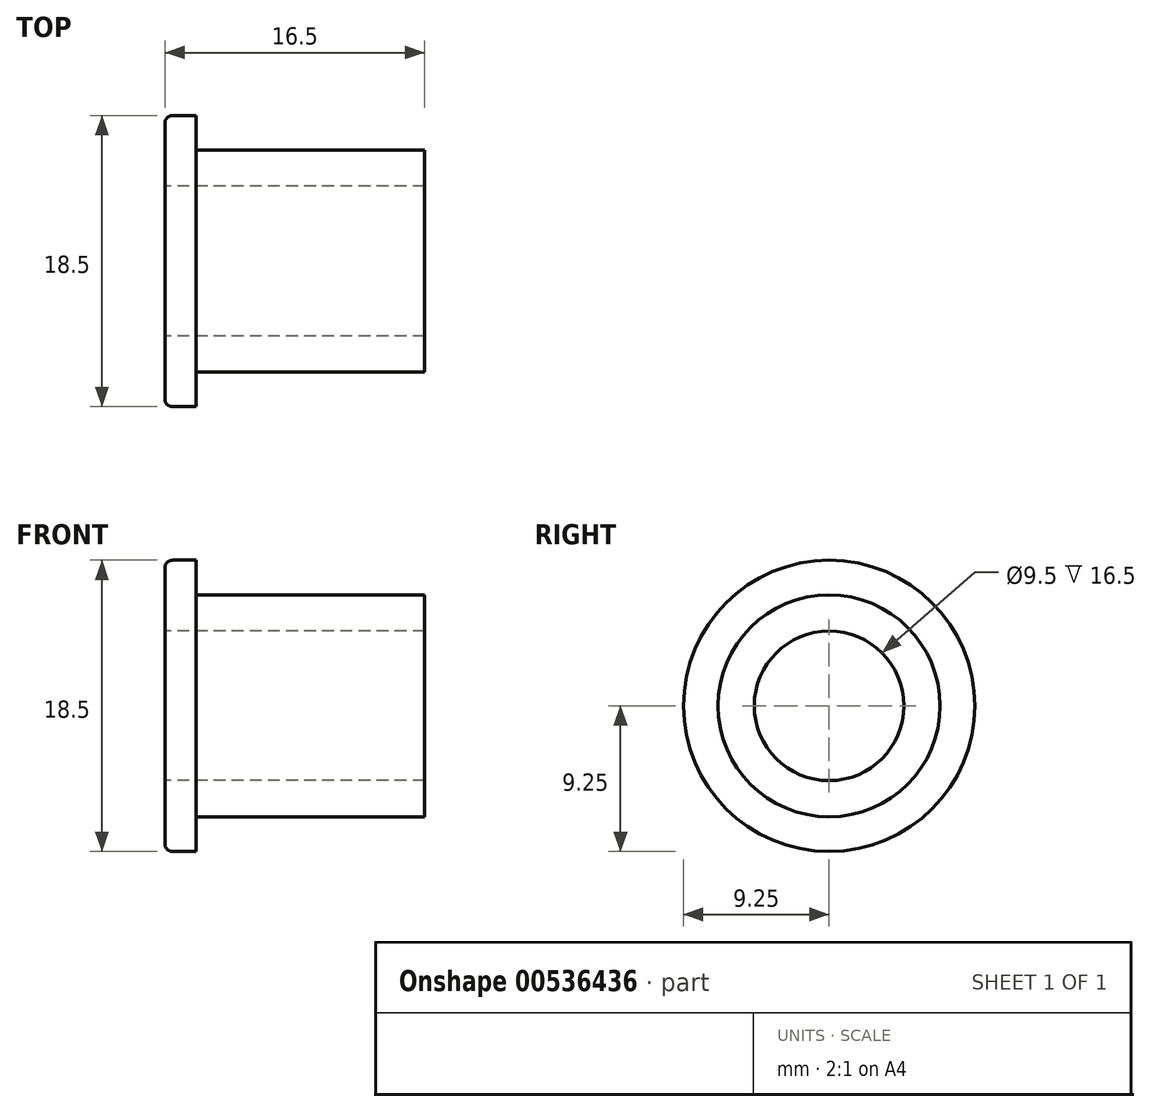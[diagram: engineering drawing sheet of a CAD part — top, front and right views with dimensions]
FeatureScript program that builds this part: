
annotation { "Feature Type Name" : "Feature", "Feature Type Description" : "" }
export const myFeature = defineFeature(function(context is Context, id is Id, definition is map)
    precondition{}
    {
        {
            var Q0;
            Q0=qCreatedBy(makeId("Front.planeOp"),FACE);
            var sketch = newSketch(context, id + "F0", { "sketchPlane" : qUnion([Q0])});
            skLineSegment(sketch, "E0", {"start": v(0, 4.75) * mm, "end": v(0, 9.25) * mm});
            skLineSegment(sketch, "E1", {"start": v(0, 9.25) * mm, "end": v(2, 9.25) * mm});
            skLineSegment(sketch, "E2", {"start": v(2, 9.25) * mm, "end": v(2, 7.05) * mm});
            skLineSegment(sketch, "E3", {"start": v(2, 7.05) * mm, "end": v(16.5, 7.05) * mm});
            skLineSegment(sketch, "E4", {"start": v(16.5, 7.05) * mm, "end": v(16.5, 4.75) * mm});
            skLineSegment(sketch, "E5", {"start": v(16.5, 4.75) * mm, "end": v(0, 4.75) * mm});
            skLineSegment(sketch, "E6", {"start": v(0, 0) * mm, "end": v(61.64, 0) * mm});
            skSolve(sketch);
        }
        {
            var Q0;
            Q0=makeQuery(id+"F0.imprint","IMPRINT",FACE,{"disambiguationData":[TD([[makeQuery(id+"F0.imprint","IMPRINT",EDGE,{"derivedFrom":sQuery(id+"F0.wireOp",EDGE,"E0")}),-1.0]])]});
            var Q1;
            Q1=sQuery(id+"F0.wireOp",EDGE,"E6");
            revolve(context, id + "F1", {"entities" : qUnion([Q0]), "axis" : qUnion([Q1]), "revolveType" : RevolveType.FULL});
        }
        {
            var Q0;
            Q0=makeQuery(id+"F1.opRevolve","SWEPT_EDGE",EDGE,{"disambiguationData":[OSD([sQuery(id+"F0.wireOp",EDGE,"E0"),sQuery(id+"F0.wireOp",EDGE,"E1")])]});
            fillet(context, id + "F2", {"entities" : qUnion([Q0]), "radius" : .5 * mm, "tangentPropagation" : true, "allowEdgeOverflow" : false});
        }
    });
